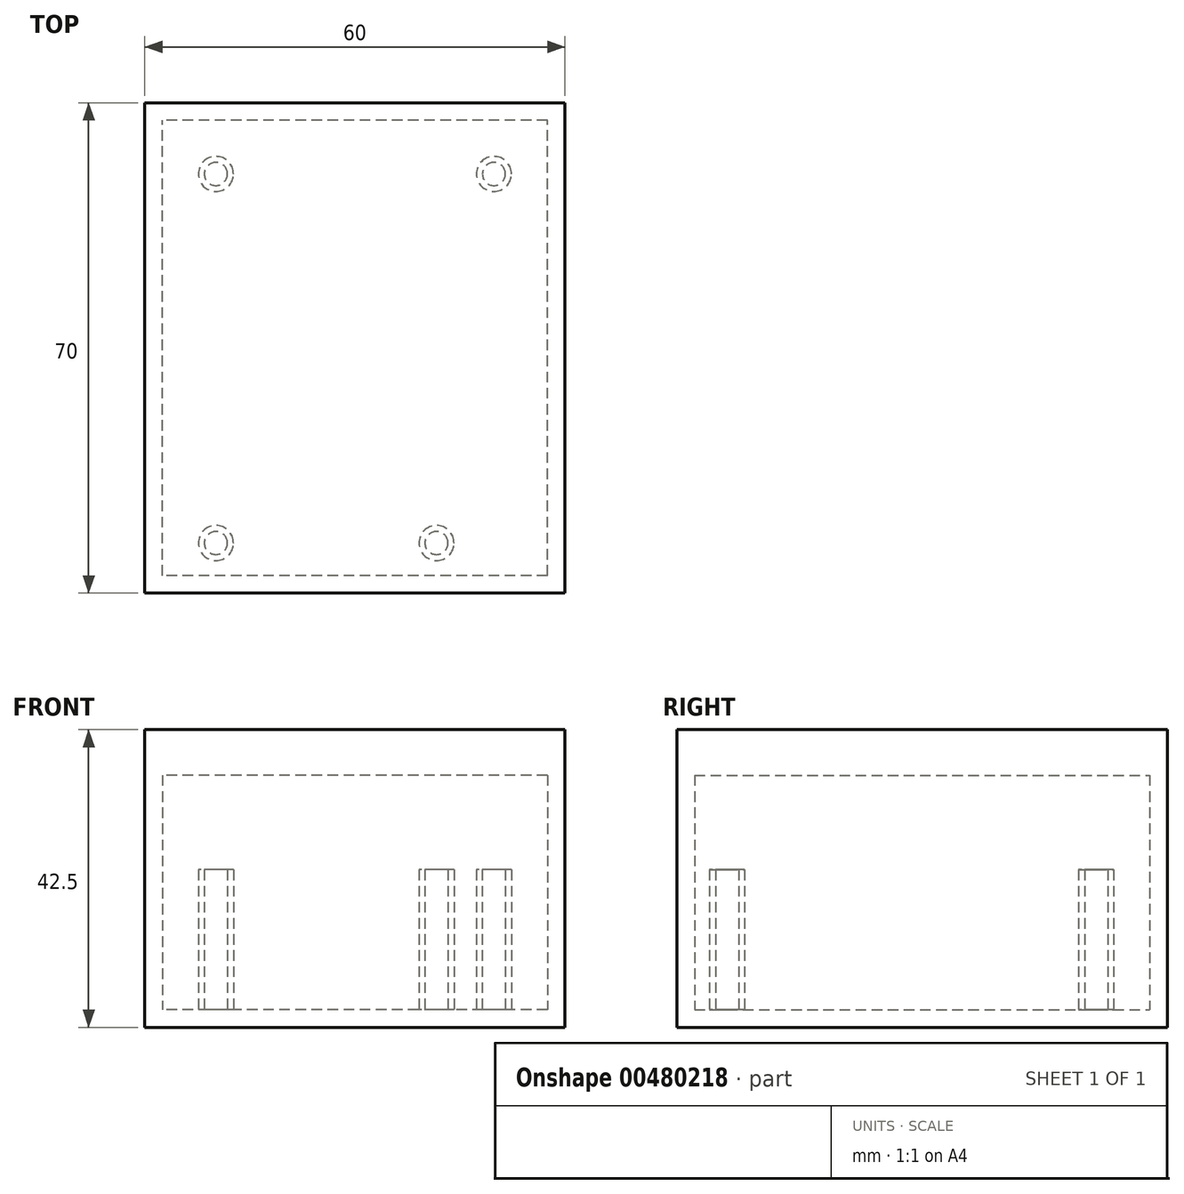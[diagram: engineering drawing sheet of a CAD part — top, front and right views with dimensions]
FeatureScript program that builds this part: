
annotation { "Feature Type Name" : "Feature", "Feature Type Description" : "" }
export const myFeature = defineFeature(function(context is Context, id is Id, definition is map)
    precondition{}
    {
        {
            assignVariable(context, id + "F0", {"name" : "high", "anyValue" : 40});
        }
        {
            var Q0;
            Q0=qCreatedBy(makeId("Top.planeOp"),FACE);
            var sketch = newSketch(context, id + "F1", { "sketchPlane" : qUnion([Q0])});
            skLineSegment(sketch, "E0.bottom", {"start": v(30, -35) * mm, "end": v(-30, -35) * mm});
            skLineSegment(sketch, "E0.top", {"start": v(30, 35) * mm, "end": v(-30, 35) * mm});
            skLineSegment(sketch, "E0.left", {"start": v(30, -35) * mm, "end": v(30, 35) * mm});
            skLineSegment(sketch, "E0.right", {"start": v(-30, -35) * mm, "end": v(-30, 35) * mm});
            skPoint(sketch, "E0.middle", {"position": v(0, 0) * mm});
            skSolve(sketch);
        }
        {
            var Q0;
            Q0 = qSketchRegion(id + "F1", true);
            extrude(context, id + "F2", {"entities" : qUnion([Q0]), "depth" : (getVariable(context, 'high')) * mm});
        }
        {
            var Q0;
            Q0=makeQuery(id+"F2.opExtrude","CAP_FACE",FACE,{"disambiguationData":[OSD([sQuery(id+"F1.wireOp",EDGE,"E0.bottom"),sQuery(id+"F1.wireOp",EDGE,"E0.top"),sQuery(id+"F1.wireOp",EDGE,"E0.left"),sQuery(id+"F1.wireOp",EDGE,"E0.right")])],"isStart":false});
            shell(context, id + "F3", {"entities" : qUnion([Q0]), "thickness" : 2.5 * mm});
        }
        {
            var Q0;
            Q0=makeQuery(id+"F2.opExtrude","CAP_FACE",FACE,{"disambiguationData":[OSD([sQuery(id+"F1.wireOp",EDGE,"E0.bottom"),sQuery(id+"F1.wireOp",EDGE,"E0.top"),sQuery(id+"F1.wireOp",EDGE,"E0.left"),sQuery(id+"F1.wireOp",EDGE,"E0.right")])],"isStart":false});
            var sketch = newSketch(context, id + "F4", { "sketchPlane" : qUnion([Q0])});
            skLineSegment(sketch, "E1.bottom", {"start": v(-27.5, 32.5) * mm, "end": v(27.5, 32.5) * mm});
            skLineSegment(sketch, "E1.top", {"start": v(-27.5, -32.5) * mm, "end": v(27.5, -32.5) * mm});
            skLineSegment(sketch, "E1.left", {"start": v(-27.5, 32.5) * mm, "end": v(-27.5, -32.5) * mm});
            skLineSegment(sketch, "E1.right", {"start": v(27.5, 32.5) * mm, "end": v(27.5, -32.5) * mm});
            skLineSegment(sketch, "E2.bottom", {"start": v(-30, 35) * mm, "end": v(30, 35) * mm});
            skLineSegment(sketch, "E2.top", {"start": v(-30, -35) * mm, "end": v(30, -35) * mm});
            skLineSegment(sketch, "E2.left", {"start": v(-30, 35) * mm, "end": v(-30, -35) * mm});
            skLineSegment(sketch, "E2.right", {"start": v(30, 35) * mm, "end": v(30, -35) * mm});
            skSolve(sketch);
        }
        {
            var Q0;
            Q0=makeQuery(id+"F4.imprint","IMPRINT",FACE,{"disambiguationData":[TD([[makeQuery(id+"F4.imprint","IMPRINT",EDGE,{"derivedFrom":sQuery(id+"F4.wireOp",EDGE,"E1.bottom")}),-1.0]])]});
            var Q1;
            Q1=makeQuery(id+"F4.imprint","IMPRINT",FACE,{"disambiguationData":[TD([[makeQuery(id+"F4.imprint","IMPRINT",EDGE,{"derivedFrom":sQuery(id+"F4.wireOp",EDGE,"E1.bottom")}),1.0]])]});
            extrude(context, id + "F5", {"entities" : qUnion([Q0, Q1]), "depth" : 2.5 * mm});
        }
        {
            var Q0;
            Q0=makeQuery(id+"F4.imprint","IMPRINT",FACE,{"disambiguationData":[TD([[makeQuery(id+"F4.imprint","IMPRINT",EDGE,{"derivedFrom":sQuery(id+"F4.wireOp",EDGE,"E1.bottom")}),1.0]])]});
            extrude(context, id + "F6", {"entities" : qUnion([Q0]), "operationType" : NewBodyOperationType.ADD, "oppositeDirection" : true, "depth" : 4 * mm});
        }
        {
            var Q0;
            Q0=makeQuery(id+"F3.opShell","OFFSET_FACE",FACE,{"disambiguationData":[OSD([sQuery(id+"F1.wireOp",EDGE,"E0.bottom"),sQuery(id+"F1.wireOp",EDGE,"E0.top"),sQuery(id+"F1.wireOp",EDGE,"E0.left"),sQuery(id+"F1.wireOp",EDGE,"E0.right")])]});
            var sketch = newSketch(context, id + "F7", { "sketchPlane" : qUnion([Q0])});
            skCircle(sketch, "E3", {"center": v(-19.85, 24.85) * mm, "radius": 1.65 * mm});
            skCircle(sketch, "E4.MirrorC", {"center": v(19.85, 24.85) * mm, "radius": 1.65 * mm});
            skCircle(sketch, "E5", {"center": v(-19.85, -27.85) * mm, "radius": 1.65 * mm});
            skCircle(sketch, "E6", {"center": v(11.65, -27.85) * mm, "radius": 1.65 * mm});
            skCircle(sketch, "E7", {"center": v(-19.85, 24.85) * mm, "radius": 2.5 * mm});
            skCircle(sketch, "E8.MirrorC", {"center": v(19.85, 24.85) * mm, "radius": 2.5 * mm});
            skCircle(sketch, "E9", {"center": v(-19.85, -27.85) * mm, "radius": 2.5 * mm});
            skCircle(sketch, "E10", {"center": v(11.65, -27.85) * mm, "radius": 2.5 * mm});
            skSolve(sketch);
        }
        {
            var Q0;
            Q0 = qSketchRegion(id + "F7", true);
            extrude(context, id + "F8", {"entities" : qUnion([Q0]), "operationType" : NewBodyOperationType.ADD, "depth" : 20 * mm});
        }
    });
